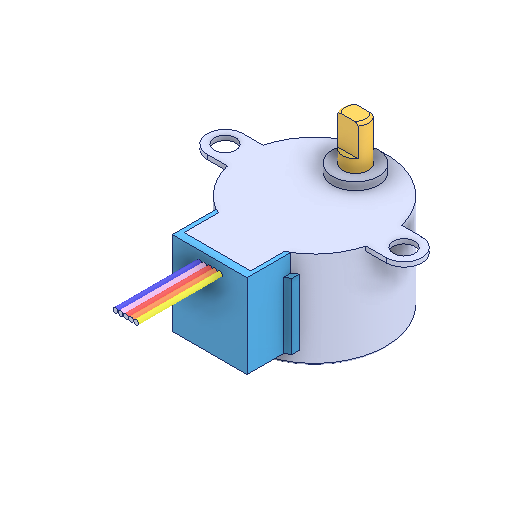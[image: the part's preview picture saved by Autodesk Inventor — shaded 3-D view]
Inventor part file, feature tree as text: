
AUTODESK INVENTOR PART (.ipt)
format: ipt  version: 2022 (Build 260153000, 153)  size: 182,784 bytes
history: native  units: mm
features: other x1, fillet x1
ambient origin geometry x8: Origin, YZ Plane, XZ Plane, XY Plane, X Axis, Y Axis, Z Axis, Center Point
bodies: Body1 (feature_tree)
feature tree (2):
  other  "Твердое тело1"
  fillet  "Fillet2"  [1 undecoded]
note: 1 required parameter value undecoded (feature->parameter linkage not recoverable at this tier; creation-order binding heuristic only, values carry confidence <= 0.55)
